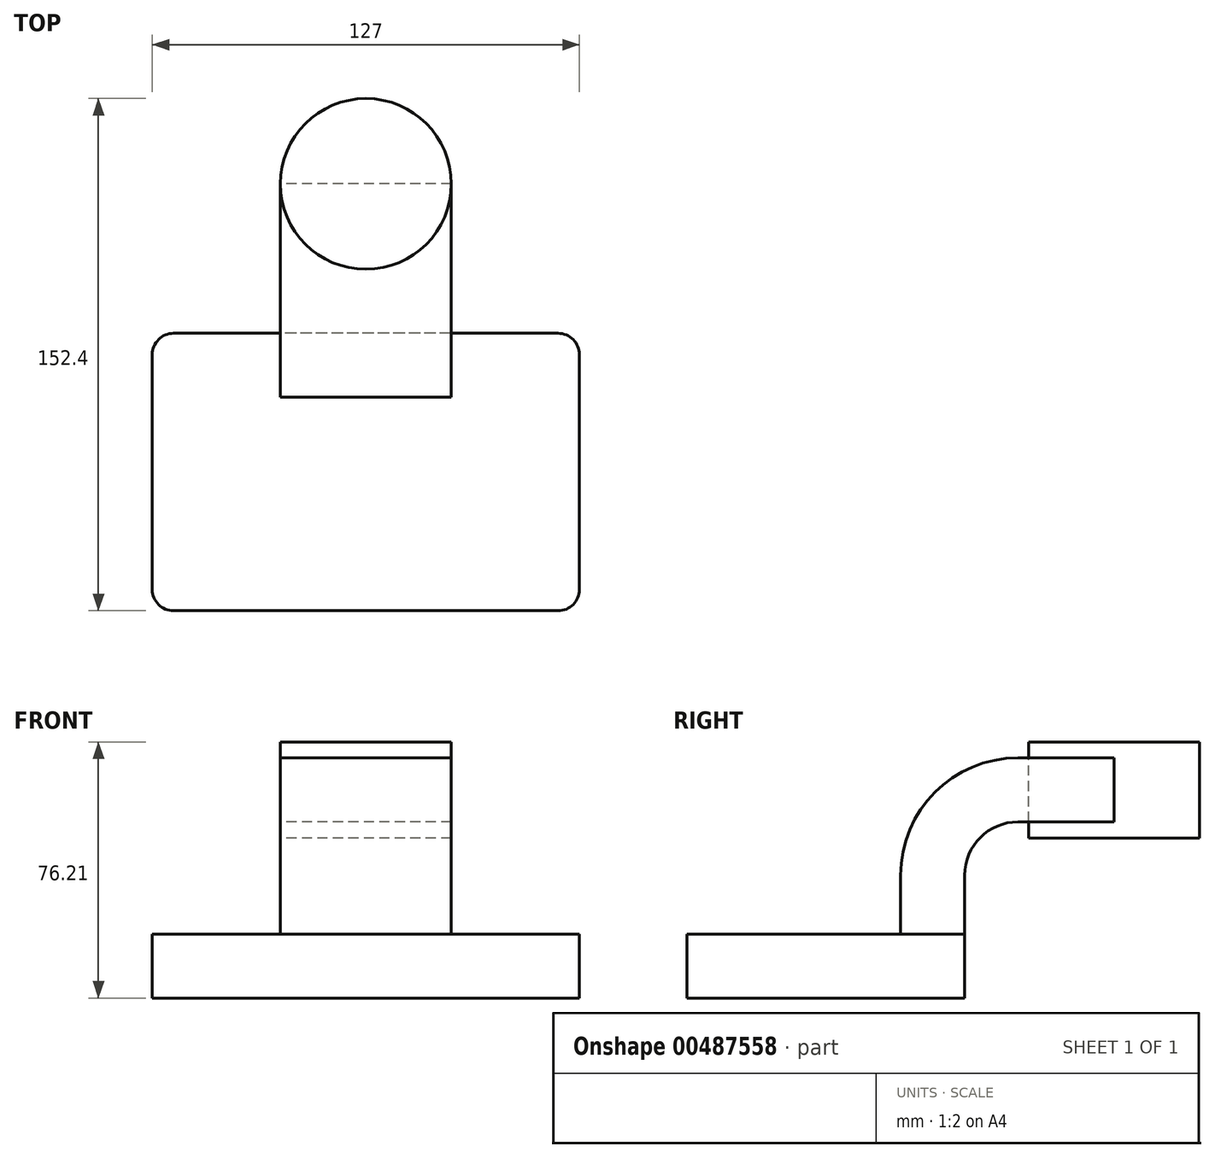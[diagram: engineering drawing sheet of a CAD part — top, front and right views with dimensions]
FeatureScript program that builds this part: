
annotation { "Feature Type Name" : "Feature", "Feature Type Description" : "" }
export const myFeature = defineFeature(function(context is Context, id is Id, definition is map)
    precondition{}
    {
        {
            var Q0;
            Q0=qCreatedBy(makeId("Right.planeOp"),FACE);
            var sketch = newSketch(context, id + "F0", { "sketchPlane" : qUnion([Q0])});
            skLineSegment(sketch, "E0.bottom", {"start": v(41.28, 9.53) * mm, "end": v(-41.28, 9.52) * mm});
            skLineSegment(sketch, "E0.top", {"start": v(41.28, -9.52) * mm, "end": v(-41.28, -9.53) * mm});
            skLineSegment(sketch, "E0.left", {"start": v(41.28, 9.53) * mm, "end": v(41.28, -9.52) * mm});
            skLineSegment(sketch, "E0.right", {"start": v(-41.28, 9.52) * mm, "end": v(-41.28, -9.53) * mm});
            skPoint(sketch, "E0.middle", {"position": v(0, 0) * mm});
            skLineSegment(sketch, "E1.bottom", {"start": v(111.13, 66.68) * mm, "end": v(60.32, 66.68) * mm});
            skLineSegment(sketch, "E1.top", {"start": v(111.12, 38.1) * mm, "end": v(60.32, 38.1) * mm});
            skLineSegment(sketch, "E1.left", {"start": v(111.12, 66.68) * mm, "end": v(111.12, 38.1) * mm});
            skLineSegment(sketch, "E1.right", {"start": v(60.32, 66.68) * mm, "end": v(60.32, 38.1) * mm});
            skPoint(sketch, "E1.middle", {"position": v(85.72, 52.39) * mm});
            skLineSegment(sketch, "E2", {"start": v(41.28, 9.53) * mm, "end": v(41.28, 27) * mm});
            skArc(sketch, "E3", {"start": v(41.28, 27) * mm, "mid": v(45.92, 38.23) * mm, "end": v(57.15, 42.88) * mm});
            skLineSegment(sketch, "E4", {"start": v(57.15, 42.88) * mm, "end": v(85.72, 42.88) * mm});
            skLineSegment(sketch, "E5.0", {"start": v(57.15, 61.93) * mm, "end": v(85.72, 61.93) * mm});
            skArc(sketch, "E5.1", {"start": v(22.23, 27) * mm, "mid": v(32.45, 51.7) * mm, "end": v(57.15, 61.93) * mm});
            skLineSegment(sketch, "E5.2", {"start": v(22.23, 9.53) * mm, "end": v(22.23, 27) * mm});
            skFitSpline(sketch, "E6", {"points": [v(-41.28, 9.52) * mm, v(57.15, 61.93) * mm], "startDerivative": vector(55.8, 137.08) * mm, "endDerivative": vector(112.54, -24.78) * mm});
            skLineSegment(sketch, "E7", {"start": v(85.73, 66.68) * mm, "end": v(85.72, 38.1) * mm});
            skSolve(sketch);
        }
        {
            var Q0;
            Q0=makeQuery(id+"F0.imprint","IMPRINT",FACE,{"disambiguationData":[TD([[makeQuery(id+"F0.imprint","IMPRINT",EDGE,{"derivedFrom":sQuery(id+"F0.wireOp",EDGE,"E0.top")}),-1.0]])]});
            extrude(context, id + "F1", {"entities" : qUnion([Q0]), "endBound" : BoundingType.SYMMETRIC, "depth" : 127 * mm});
        }
        {
            var Q0;
            {var subQ1=sQuery(id+"F0.wireOp",EDGE,"E2");Q0=makeQuery(id+"F0.imprint","IMPRINT",FACE,{"disambiguationData":[TD([[makeQuery(id+"F0.imprint","IMPRINT",EDGE,{"derivedFrom":subQ1}),1.0]])]});}
            var Q1;
            {var subQ0=sQuery(id+"F0.wireOp",EDGE,"E5.0");var subQ1=sQuery(id+"F0.wireOp",EDGE,"E1.right");var subQ2=makeQuery(id+"F0.imprint","INTERSECT",VERTEX,{"derivedFrom":[subQ1,subQ0]});Q1=makeQuery(id+"F0.imprint","IMPRINT",FACE,{"disambiguationData":[TD([[makeQuery(id+"F0.imprint","IMPRINT",EDGE,{"disambiguationData":[TD([[subQ2,-1.0]])],"derivedFrom":subQ1}),1.0]])]});}
            extrude(context, id + "F2", {"entities" : qUnion([Q0, Q1]), "operationType" : NewBodyOperationType.ADD, "endBound" : BoundingType.SYMMETRIC, "depth" : 50.8 * mm});
        }
        {
            var Q0;
            Q0=makeQuery(id+"F0.imprint","IMPRINT",FACE,{"disambiguationData":[TD([[makeQuery(id+"F0.imprint","IMPRINT",EDGE,{"derivedFrom":sQuery(id+"F0.wireOp",EDGE,"E5.1")}),1.0]])]});
            extrude(context, id + "F3", {"entities" : qUnion([Q0]), "operationType" : NewBodyOperationType.ADD, "endBound" : BoundingType.SYMMETRIC, "depth" : 15.88 * mm});
        }
        {
            var Q0;
            {var subQ0=sQuery(id+"F0.wireOp",EDGE,"E1.left");Q0=makeQuery(id+"F0.imprint","IMPRINT",FACE,{"disambiguationData":[TD([[makeQuery(id+"F0.imprint","IMPRINT",EDGE,{"derivedFrom":subQ0}),-1.0]])]});}
            var Q1;
            Q1=sQuery(id+"F0.wireOp",EDGE,"E7");
            revolve(context, id + "F4", {"entities" : qUnion([Q0]), "axis" : qUnion([Q1]), "revolveType" : RevolveType.FULL});
        }
        {
            var Q0;
            Q0=makeQuery(id+"F1.opExtrude","CAP_EDGE",EDGE,{"disambiguationData":[OSD([sQuery(id+"F0.wireOp",EDGE,"E0.right")])],"isStart":false});
            var Q1;
            Q1=makeQuery(id+"F1.opExtrude","CAP_EDGE",EDGE,{"disambiguationData":[OSD([sQuery(id+"F0.wireOp",EDGE,"E0.left")])],"isStart":false});
            var Q2;
            Q2=makeQuery(id+"F1.opExtrude","CAP_EDGE",EDGE,{"disambiguationData":[OSD([sQuery(id+"F0.wireOp",EDGE,"E0.right")])],"isStart":true});
            var Q3;
            Q3=makeQuery(id+"F1.opExtrude","CAP_EDGE",EDGE,{"disambiguationData":[OSD([sQuery(id+"F0.wireOp",EDGE,"E0.left")])],"isStart":true});
            fillet(context, id + "F5", {"entities" : qUnion([Q0, Q1, Q2, Q3]), "radius" : 6.35 * mm, "tangentPropagation" : true, "allowEdgeOverflow" : false});
        }
    });
